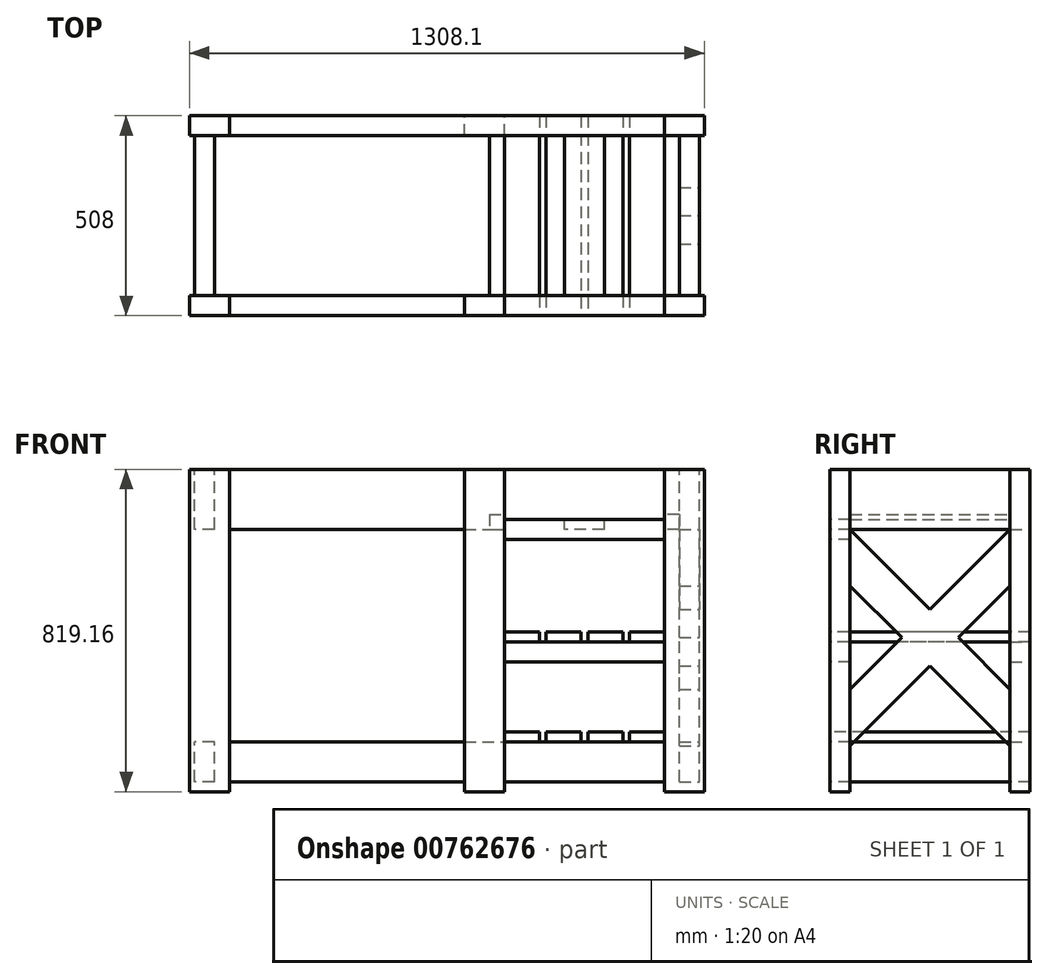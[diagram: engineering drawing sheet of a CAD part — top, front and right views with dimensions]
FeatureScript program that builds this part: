
annotation { "Feature Type Name" : "Feature", "Feature Type Description" : "" }
export const myFeature = defineFeature(function(context is Context, id is Id, definition is map)
    precondition{}
    {
        {
            var Q0;
            Q0=qCreatedBy(makeId("Right.planeOp"),FACE);
            var sketch = newSketch(context, id + "F0", { "sketchPlane" : qUnion([Q0])});
            skLineSegment(sketch, "E0.bottom", {"start": v(-254, 409.58) * mm, "end": v(-203.2, 409.58) * mm});
            skLineSegment(sketch, "E0.top", {"start": v(-254, -409.58) * mm, "end": v(-203.2, -409.58) * mm});
            skLineSegment(sketch, "E0.left", {"start": v(-254, 409.58) * mm, "end": v(-254, -409.58) * mm});
            skLineSegment(sketch, "E0.right", {"start": v(-203.2, 409.58) * mm, "end": v(-203.2, -409.58) * mm});
            skLineSegment(sketch, "E1.bottom", {"start": v(203.2, -409.58) * mm, "end": v(254, -409.58) * mm});
            skLineSegment(sketch, "E1.top", {"start": v(203.2, 409.58) * mm, "end": v(254, 409.58) * mm});
            skLineSegment(sketch, "E1.left", {"start": v(203.2, -409.58) * mm, "end": v(203.2, 409.58) * mm});
            skLineSegment(sketch, "E1.right", {"start": v(254, -409.58) * mm, "end": v(254, 409.58) * mm});
            skSolve(sketch);
        }
        {
            var Q0;
            Q0 = qSketchRegion(id + "F0", true);
            extrude(context, id + "F1", {"entities" : qUnion([Q0]), "depth" : 101.6 * mm, "offsetDistance" : 25.4 * mm});
        }
        {
            var Q0;
            Q0=makeQuery(id+"F1.opExtrude","SWEPT_FACE",FACE,{"disambiguationData":[OSD([sQuery(id+"F0.wireOp",EDGE,"E0.right")])]});
            var sketch = newSketch(context, id + "F2", { "sketchPlane" : qUnion([Q0])});
            skLineSegment(sketch, "E2.bottom", {"start": v(-88.9, 409.58) * mm, "end": v(-38.1, 409.58) * mm});
            skLineSegment(sketch, "E2.top", {"start": v(-88.9, 257.18) * mm, "end": v(-38.1, 257.18) * mm});
            skLineSegment(sketch, "E2.left", {"start": v(-88.9, 409.58) * mm, "end": v(-88.9, 257.18) * mm});
            skLineSegment(sketch, "E2.right", {"start": v(-38.1, 409.58) * mm, "end": v(-38.1, 257.18) * mm});
            skLineSegment(sketch, "E3.bottom", {"start": v(-88.9, -282.58) * mm, "end": v(-38.1, -282.58) * mm});
            skLineSegment(sketch, "E3.top", {"start": v(-88.9, -384.18) * mm, "end": v(-38.1, -384.18) * mm});
            skLineSegment(sketch, "E3.right", {"start": v(-38.1, -282.58) * mm, "end": v(-38.1, -384.18) * mm});
            skLineSegment(sketch, "E4", {"start": v(-88.9, -282.58) * mm, "end": v(-88.9, -384.18) * mm});
            skSolve(sketch);
        }
        {
            var Q0;
            Q0 = qSketchRegion(id + "F2", true);
            extrude(context, id + "F3", {"entities" : qUnion([Q0]), "endBound" : BoundingType.UP_TO_NEXT, "depth" : 25.4 * mm, "offsetDistance" : 25.4 * mm});
        }
        {
            var Q0;
            Q0=makeQuery(id+"F3.opExtrude","SWEPT_FACE",FACE,{"disambiguationData":[OSD([sQuery(id+"F2.wireOp",EDGE,"E2.left")])]});
            var sketch = newSketch(context, id + "F4", { "sketchPlane" : qUnion([Q0])});
            skLineSegment(sketch, "E5", {"start": v(-203.2, 257.18) * mm, "end": v(-203.2, 113.5) * mm});
            skLineSegment(sketch, "E6", {"start": v(-203.2, 113.5) * mm, "end": v(203.2, -292.9) * mm});
            skLineSegment(sketch, "E7", {"start": v(203.2, -292.9) * mm, "end": v(203.2, -149.22) * mm});
            skLineSegment(sketch, "E8", {"start": v(203.2, -149.22) * mm, "end": v(-203.2, 257.18) * mm});
            skLineSegment(sketch, "E9", {"start": v(203.2, 257.18) * mm, "end": v(0, 53.98) * mm});
            skLineSegment(sketch, "E10", {"start": v(-203.2, -149.22) * mm, "end": v(-203.2, -292.9) * mm});
            skLineSegment(sketch, "E11", {"start": v(-203.2, -292.9) * mm, "end": v(0, -89.7) * mm});
            skLineSegment(sketch, "E12", {"start": v(203.2, 113.5) * mm, "end": v(203.2, 257.18) * mm});
            skLineSegment(sketch, "E13.trimOffspring", {"start": v(-71.84, -17.87) * mm, "end": v(-203.2, -149.22) * mm});
            skLineSegment(sketch, "E14.trimOffspring", {"start": v(71.84, -17.87) * mm, "end": v(203.2, 113.5) * mm});
            skSolve(sketch);
        }
        {
            var Q0;
            Q0 = qSketchRegion(id + "F4", true);
            extrude(context, id + "F5", {"entities" : qUnion([Q0]), "oppositeDirection" : true, "depth" : 50.8 * mm, "offsetDistance" : 25.4 * mm});
        }
        {
            var Q0;
            Q0=makeQuery(id+"F1.opExtrude","CAP_FACE",FACE,{"disambiguationData":[OSD([sQuery(id+"F0.wireOp",EDGE,"E0.bottom"),sQuery(id+"F0.wireOp",EDGE,"E0.top"),sQuery(id+"F0.wireOp",EDGE,"E0.left"),sQuery(id+"F0.wireOp",EDGE,"E0.right")])],"isStart":true});
            var sketch = newSketch(context, id + "F6", { "sketchPlane" : qUnion([Q0])});
            skLineSegment(sketch, "E15.bottom", {"start": v(203.2, -282.58) * mm, "end": v(254, -282.58) * mm});
            skLineSegment(sketch, "E15.top", {"start": v(203.2, -384.18) * mm, "end": v(254, -384.18) * mm});
            skLineSegment(sketch, "E15.left", {"start": v(203.2, -282.58) * mm, "end": v(203.2, -384.18) * mm});
            skLineSegment(sketch, "E15.right", {"start": v(254, -282.58) * mm, "end": v(254, -384.18) * mm});
            skLineSegment(sketch, "E16.bottom", {"start": v(-254, -282.58) * mm, "end": v(-203.2, -282.58) * mm});
            skLineSegment(sketch, "E16.top", {"start": v(-254, -384.18) * mm, "end": v(-203.2, -384.18) * mm});
            skLineSegment(sketch, "E16.left", {"start": v(-254, -282.58) * mm, "end": v(-254, -384.18) * mm});
            skLineSegment(sketch, "E16.right", {"start": v(-203.2, -282.58) * mm, "end": v(-203.2, -384.18) * mm});
            skSolve(sketch);
        }
        {
            var Q0;
            Q0=makeQuery(id+"F1.opExtrude","CAP_FACE",FACE,{"disambiguationData":[OSD([sQuery(id+"F0.wireOp",EDGE,"E0.bottom"),sQuery(id+"F0.wireOp",EDGE,"E0.top"),sQuery(id+"F0.wireOp",EDGE,"E0.left"),sQuery(id+"F0.wireOp",EDGE,"E0.right")])],"isStart":true});
            cPlane(context, id + "F7", {"entities" : qUnion([Q0]), "cplaneType" : CPlaneType.OFFSET, "offset" : 552.45 * mm, "width" : 152.4 * mm, "height" : 152.4 * mm});
        }
        {
            var Q0;
            Q0=makeQuery(id+"F1.opExtrude","SWEPT_BODY",BODY,{"disambiguationData":[OSD([sQuery(id+"F0.wireOp",EDGE,"E1.bottom"),sQuery(id+"F0.wireOp",EDGE,"E1.top"),sQuery(id+"F0.wireOp",EDGE,"E1.left"),sQuery(id+"F0.wireOp",EDGE,"E1.right")])]});
            var Q1;
            Q1=makeQuery(id+"F3.opExtrude","SWEPT_BODY",BODY,{"disambiguationData":[OSD([sQuery(id+"F2.wireOp",EDGE,"E2.bottom"),sQuery(id+"F2.wireOp",EDGE,"E2.top"),sQuery(id+"F2.wireOp",EDGE,"E2.left"),sQuery(id+"F2.wireOp",EDGE,"E2.right")])]});
            var Q2;
            Q2=makeQuery(id+"F1.opExtrude","SWEPT_BODY",BODY,{"disambiguationData":[OSD([sQuery(id+"F0.wireOp",EDGE,"E0.bottom"),sQuery(id+"F0.wireOp",EDGE,"E0.top"),sQuery(id+"F0.wireOp",EDGE,"E0.left"),sQuery(id+"F0.wireOp",EDGE,"E0.right")])]});
            var Q3;
            Q3=makeQuery(id+"F3.opExtrude","SWEPT_BODY",BODY,{"disambiguationData":[OSD([sQuery(id+"F2.wireOp",EDGE,"E3.bottom"),sQuery(id+"F2.wireOp",EDGE,"E3.top"),sQuery(id+"F2.wireOp",EDGE,"E3.right"),sQuery(id+"F2.wireOp",EDGE,"E4")])]});
            var Q4;
            Q4=qCreatedBy(id+"F7.planeOp",FACE);
            mirror(context, id + "F8", {"entities" : qUnion([Q0, Q1, Q2, Q3]), "mirrorPlane" : qUnion([Q4])});
        }
        {
            var Q0;
            Q0=makeQuery(id+"F1.opExtrude","CAP_FACE",FACE,{"disambiguationData":[OSD([sQuery(id+"F0.wireOp",EDGE,"E0.bottom"),sQuery(id+"F0.wireOp",EDGE,"E0.top"),sQuery(id+"F0.wireOp",EDGE,"E0.left"),sQuery(id+"F0.wireOp",EDGE,"E0.right")])],"isStart":true});
            var sketch = newSketch(context, id + "F9", { "sketchPlane" : qUnion([Q0])});
            skLineSegment(sketch, "E17.bottom", {"start": v(203.2, 282.58) * mm, "end": v(254, 282.58) * mm});
            skLineSegment(sketch, "E17.top", {"start": v(203.2, 231.78) * mm, "end": v(254, 231.78) * mm});
            skLineSegment(sketch, "E17.left", {"start": v(203.2, 282.58) * mm, "end": v(203.2, 231.78) * mm});
            skLineSegment(sketch, "E17.right", {"start": v(254, 282.58) * mm, "end": v(254, 231.78) * mm});
            skLineSegment(sketch, "E18.bottom", {"start": v(203.2, 409.58) * mm, "end": v(254, 409.58) * mm});
            skLineSegment(sketch, "E18.top", {"start": v(203.2, 384.18) * mm, "end": v(254, 384.18) * mm});
            skLineSegment(sketch, "E18.left", {"start": v(203.2, 409.58) * mm, "end": v(203.2, 384.18) * mm});
            skLineSegment(sketch, "E18.right", {"start": v(254, 409.58) * mm, "end": v(254, 384.18) * mm});
            skLineSegment(sketch, "E19.bottom", {"start": v(-254, 409.58) * mm, "end": v(-203.2, 409.58) * mm});
            skLineSegment(sketch, "E19.top", {"start": v(-254, 384.18) * mm, "end": v(-203.2, 384.18) * mm});
            skLineSegment(sketch, "E19.left", {"start": v(-254, 409.58) * mm, "end": v(-254, 384.18) * mm});
            skLineSegment(sketch, "E19.right", {"start": v(-203.2, 409.58) * mm, "end": v(-203.2, 384.18) * mm});
            skPoint(sketch, "E20", {"position": v(254, 257.18) * mm});
            skLineSegment(sketch, "E21.bottom", {"start": v(203.2, -28.57) * mm, "end": v(254, -28.57) * mm});
            skLineSegment(sketch, "E21.top", {"start": v(203.2, -79.37) * mm, "end": v(254, -79.37) * mm});
            skLineSegment(sketch, "E21.left", {"start": v(203.2, -28.57) * mm, "end": v(203.2, -79.37) * mm});
            skLineSegment(sketch, "E21.right", {"start": v(254, -28.57) * mm, "end": v(254, -79.37) * mm});
            skLineSegment(sketch, "E22.bottom", {"start": v(-203.2, -28.57) * mm, "end": v(-254, -28.57) * mm});
            skLineSegment(sketch, "E22.top", {"start": v(-203.2, -79.37) * mm, "end": v(-254, -79.37) * mm});
            skLineSegment(sketch, "E22.left", {"start": v(-203.2, -28.57) * mm, "end": v(-203.2, -79.37) * mm});
            skLineSegment(sketch, "E22.right", {"start": v(-254, -28.57) * mm, "end": v(-254, -79.37) * mm});
            skSolve(sketch);
        }
        {
            var Q0;
            Q0=makeQuery(id+"F9.imprint","IMPRINT",FACE,{"disambiguationData":[TD([[makeQuery(id+"F9.imprint","IMPRINT",EDGE,{"derivedFrom":sQuery(id+"F9.wireOp",EDGE,"KkQRvC9S-9GU5-1TNo-BgkX-bVCRlUlDrE3p.bottom")}),-1.0]])]});
            var Q1;
            Q1=makeQuery(id+"F9.imprint","IMPRINT",FACE,{"disambiguationData":[TD([[makeQuery(id+"F9.imprint","IMPRINT",EDGE,{"derivedFrom":sQuery(id+"F9.wireOp",EDGE,"E17.bottom")}),-1.0]])]});
            var Q2;
            Q2=makeQuery(id+"F9.imprint","IMPRINT",FACE,{"disambiguationData":[TD([[makeQuery(id+"F9.imprint","IMPRINT",EDGE,{"derivedFrom":sQuery(id+"F9.wireOp",EDGE,"E21.bottom")}),-1.0]])]});
            var Q3;
            Q3=makeQuery(id+"F9.imprint","IMPRINT",FACE,{"disambiguationData":[TD([[makeQuery(id+"F9.imprint","IMPRINT",EDGE,{"derivedFrom":sQuery(id+"F9.wireOp",EDGE,"E22.bottom")}),1.0]])]});
            extrude(context, id + "F10", {"entities" : qUnion([Q0, Q1, Q2, Q3]), "depth" : 406.4 * mm, "offsetDistance" : 25.4 * mm});
        }
        {
            var Q0;
            Q0=makeQuery(id+"F10.opExtrude","CAP_FACE",FACE,{"disambiguationData":[OSD([sQuery(id+"F9.wireOp",EDGE,"E17.bottom"),sQuery(id+"F9.wireOp",EDGE,"E17.top"),sQuery(id+"F9.wireOp",EDGE,"E17.left"),sQuery(id+"F9.wireOp",EDGE,"E17.right")])],"isStart":false});
            var sketch = newSketch(context, id + "F11", { "sketchPlane" : qUnion([Q0])});
            skLineSegment(sketch, "E23.top", {"start": v(254, 409.58) * mm, "end": v(203.2, 409.58) * mm});
            skLineSegment(sketch, "E23.left", {"start": v(254, -409.58) * mm, "end": v(254, 409.57) * mm});
            skLineSegment(sketch, "E23.right", {"start": v(203.2, -409.58) * mm, "end": v(203.2, 409.58) * mm});
            skLineSegment(sketch, "E24.bottom", {"start": v(-203.2, -282.58) * mm, "end": v(-254, -282.58) * mm});
            skLineSegment(sketch, "E24.top", {"start": v(-203.2, 257.18) * mm, "end": v(-254, 257.18) * mm});
            skLineSegment(sketch, "E24.left", {"start": v(-203.2, -282.58) * mm, "end": v(-203.2, 257.18) * mm});
            skLineSegment(sketch, "E24.right", {"start": v(-254, -282.58) * mm, "end": v(-254, 257.18) * mm});
            skLineSegment(sketch, "E25", {"start": v(203.2, -409.58) * mm, "end": v(254, -409.58) * mm});
            skSolve(sketch);
        }
        {
            var Q0;
            Q0=makeQuery(id+"F6.imprint","IMPRINT",FACE,{"disambiguationData":[TD([[makeQuery(id+"F6.imprint","IMPRINT",EDGE,{"derivedFrom":sQuery(id+"F6.wireOp",EDGE,"E16.bottom")}),-1.0]])]});
            extrude(context, id + "F12", {"entities" : qUnion([Q0]), "endBound" : BoundingType.UP_TO_NEXT, "depth" : 25.4 * mm, "offsetDistance" : 25.4 * mm});
        }
        {
            var Q0;
            Q0 = qSketchRegion(id + "F11", true);
            extrude(context, id + "F13", {"entities" : qUnion([Q0]), "depth" : 101.6 * mm, "offsetDistance" : 25.4 * mm});
        }
        {
            var Q0;
            Q0=makeQuery(id+"Fzglu1UX7R0Jx5i_16.boolean.opBoolean","MERGE",FACE,{"derivedFrom":[makeQuery(id+"F1.opExtrude","SWEPT_FACE",FACE,{"disambiguationData":[OSD([sQuery(id+"F0.wireOp",EDGE,"E0.left")])]}),makeQuery(id+"Fzglu1UX7R0Jx5i_16.opExtrude","SWEPT_FACE",FACE,{"disambiguationData":[OSD([sQuery(id+"F6.wireOp",EDGE,"E15.right")])]})]});
            var sketch = newSketch(context, id + "F14", { "sketchPlane" : qUnion([Q0])});
            skLineSegment(sketch, "E26.bottom", {"start": v(0, -3.17) * mm, "end": v(-88.9, -3.17) * mm});
            skLineSegment(sketch, "E26.top", {"start": v(0, -28.57) * mm, "end": v(-88.9, -28.57) * mm});
            skLineSegment(sketch, "E26.left", {"start": v(0, -3.17) * mm, "end": v(0, -28.57) * mm});
            skLineSegment(sketch, "E26.right", {"start": v(-406.4, -3.17) * mm, "end": v(-406.4, -28.57) * mm});
            skLineSegment(sketch, "E27", {"start": v(-317.5, -3.17) * mm, "end": v(-317.5, -28.57) * mm});
            skLineSegment(sketch, "E28", {"start": v(-300.35, -3.17) * mm, "end": v(-300.35, -28.57) * mm});
            skLineSegment(sketch, "E29", {"start": v(-211.45, -3.17) * mm, "end": v(-211.45, -28.57) * mm});
            skLineSegment(sketch, "E30", {"start": v(-194.3, -3.17) * mm, "end": v(-194.3, -28.57) * mm});
            skLineSegment(sketch, "E31", {"start": v(-105.4, -3.17) * mm, "end": v(-105.4, -28.57) * mm});
            skLineSegment(sketch, "E32", {"start": v(-88.9, -3.17) * mm, "end": v(-88.9, -28.57) * mm});
            skLineSegment(sketch, "E33.trimOffspring", {"start": v(-317.5, -3.17) * mm, "end": v(-406.4, -3.17) * mm});
            skLineSegment(sketch, "E34.trimOffspring", {"start": v(-317.5, -28.57) * mm, "end": v(-406.4, -28.57) * mm});
            skLineSegment(sketch, "E35.trimOffspring", {"start": v(-211.45, -3.17) * mm, "end": v(-300.35, -3.17) * mm});
            skLineSegment(sketch, "E36.trimOffspring", {"start": v(-211.45, -28.57) * mm, "end": v(-300.35, -28.57) * mm});
            skLineSegment(sketch, "E37.trimOffspring", {"start": v(-105.4, -3.17) * mm, "end": v(-194.3, -3.17) * mm});
            skLineSegment(sketch, "E38.trimOffspring", {"start": v(-105.4, -28.57) * mm, "end": v(-194.3, -28.57) * mm});
            skLineSegment(sketch, "E39.bottom", {"start": v(0, -257.18) * mm, "end": v(-88.9, -257.18) * mm});
            skLineSegment(sketch, "E39.top", {"start": v(0, -282.58) * mm, "end": v(-88.9, -282.58) * mm});
            skLineSegment(sketch, "E39.left", {"start": v(0, -257.18) * mm, "end": v(0, -282.58) * mm});
            skLineSegment(sketch, "E39.right", {"start": v(-406.4, -257.18) * mm, "end": v(-406.4, -282.58) * mm});
            skLineSegment(sketch, "E40", {"start": v(-317.5, -257.18) * mm, "end": v(-317.5, -282.58) * mm});
            skLineSegment(sketch, "E41", {"start": v(-300.35, -257.18) * mm, "end": v(-300.35, -282.58) * mm});
            skLineSegment(sketch, "E42", {"start": v(-211.45, -257.18) * mm, "end": v(-211.45, -282.58) * mm});
            skLineSegment(sketch, "E43", {"start": v(-194.3, -257.18) * mm, "end": v(-194.3, -282.58) * mm});
            skLineSegment(sketch, "E44", {"start": v(-105.4, -257.18) * mm, "end": v(-105.4, -282.58) * mm});
            skLineSegment(sketch, "E45", {"start": v(-88.9, -257.18) * mm, "end": v(-88.9, -282.58) * mm});
            skLineSegment(sketch, "E46.trimOffspring", {"start": v(-317.5, -257.18) * mm, "end": v(-406.4, -257.18) * mm});
            skLineSegment(sketch, "E47.trimOffspring", {"start": v(-317.5, -282.58) * mm, "end": v(-406.4, -282.58) * mm});
            skLineSegment(sketch, "E48.trimOffspring", {"start": v(-211.45, -257.18) * mm, "end": v(-300.35, -257.18) * mm});
            skLineSegment(sketch, "E49.trimOffspring", {"start": v(-211.45, -282.58) * mm, "end": v(-300.35, -282.58) * mm});
            skLineSegment(sketch, "E50.trimOffspring", {"start": v(-105.4, -257.18) * mm, "end": v(-194.3, -257.18) * mm});
            skLineSegment(sketch, "E51.trimOffspring", {"start": v(-105.4, -282.58) * mm, "end": v(-194.3, -282.58) * mm});
            skSolve(sketch);
        }
        {
            var Q0;
            Q0 = qSketchRegion(id + "F14", true);
            var Q1;
            Q1=makeQuery(id+"F1.opExtrude","SWEPT_FACE",FACE,{"disambiguationData":[OSD([sQuery(id+"F0.wireOp",EDGE,"E1.right")])]});
            extrude(context, id + "F15", {"entities" : qUnion([Q0]), "endBound" : BoundingType.UP_TO_SURFACE, "oppositeDirection" : true, "depth" : 25.4 * mm, "endBoundEntityFace" : qUnion([Q1]), "offsetDistance" : 25.4 * mm});
        }
        {
            var Q0;
            Q0=makeQuery(id+"F6.imprint","IMPRINT",FACE,{"disambiguationData":[TD([[makeQuery(id+"F6.imprint","IMPRINT",EDGE,{"derivedFrom":sQuery(id+"F6.wireOp",EDGE,"E15.bottom")}),-1.0]])]});
            extrude(context, id + "F16", {"entities" : qUnion([Q0]), "endBound" : BoundingType.UP_TO_NEXT, "depth" : 25.4 * mm, "offsetDistance" : 25.4 * mm});
        }
        {
            var Q0;
            Q0=makeQuery(id+"F8.opPattern","COPY",FACE,{"derivedFrom":makeQuery(id+"F1.opExtrude","CAP_FACE",FACE,{"disambiguationData":[OSD([sQuery(id+"F0.wireOp",EDGE,"E0.bottom"),sQuery(id+"F0.wireOp",EDGE,"E0.top"),sQuery(id+"F0.wireOp",EDGE,"E0.left"),sQuery(id+"F0.wireOp",EDGE,"E0.right")])],"isStart":true}),"instanceName":"1"});
            var sketch = newSketch(context, id + "F17", { "sketchPlane" : qUnion([Q0])});
            skLineSegment(sketch, "E52.bottom", {"start": v(-254, 257.18) * mm, "end": v(-203.2, 257.18) * mm});
            skLineSegment(sketch, "E52.top", {"start": v(-254, 409.58) * mm, "end": v(-203.2, 409.58) * mm});
            skLineSegment(sketch, "E52.left", {"start": v(-254, 257.18) * mm, "end": v(-254, 409.58) * mm});
            skLineSegment(sketch, "E53.bottom", {"start": v(203.2, 409.58) * mm, "end": v(254, 409.58) * mm});
            skLineSegment(sketch, "E53.top", {"start": v(203.2, 257.18) * mm, "end": v(254, 257.18) * mm});
            skLineSegment(sketch, "E53.left", {"start": v(203.2, 409.58) * mm, "end": v(203.2, 257.18) * mm});
            skLineSegment(sketch, "E53.right", {"start": v(254, 409.58) * mm, "end": v(254, 257.18) * mm});
            skSolve(sketch);
        }
        {
            var Q0;
            Q0=makeQuery(id+"F17.imprint","IMPRINT",FACE,{"disambiguationData":[TD([[makeQuery(id+"F17.imprint","IMPRINT",EDGE,{"derivedFrom":sQuery(id+"F17.wireOp",EDGE,"E52.bottom")}),1.0]])]});
            extrude(context, id + "F18", {"entities" : qUnion([Q0]), "endBound" : BoundingType.UP_TO_NEXT, "depth" : 25.4 * mm, "offsetDistance" : 25.4 * mm});
        }
        {
            var Q0;
            Q0=makeQuery(id+"F17.imprint","IMPRINT",FACE,{"disambiguationData":[TD([[makeQuery(id+"F17.imprint","IMPRINT",EDGE,{"derivedFrom":sQuery(id+"F17.wireOp",EDGE,"E53.bottom")}),-1.0]])]});
            extrude(context, id + "F19", {"entities" : qUnion([Q0]), "endBound" : BoundingType.UP_TO_NEXT, "depth" : 25.4 * mm, "offsetDistance" : 25.4 * mm});
        }
        {
            var Q0;
            Q0=makeQuery(id+"F19.opExtrude","SWEPT_FACE",FACE,{"disambiguationData":[OSD([sQuery(id+"F17.wireOp",EDGE,"E53.left")])]});
            var sketch = newSketch(context, id + "F20", { "sketchPlane" : qUnion([Q0])});
            skLineSegment(sketch, "E54.bottom", {"start": v(-254, 257.18) * mm, "end": v(-152.4, 257.18) * mm});
            skLineSegment(sketch, "E54.top", {"start": v(-254, 282.58) * mm, "end": v(-152.4, 282.58) * mm});
            skLineSegment(sketch, "E54.left", {"start": v(-254, 257.18) * mm, "end": v(-254, 282.58) * mm});
            skLineSegment(sketch, "E54.right", {"start": v(-152.4, 257.18) * mm, "end": v(-152.4, 282.58) * mm});
            skPoint(sketch, "E55", {"position": v(-203.2, 282.58) * mm});
            skLineSegment(sketch, "E56.bottom", {"start": v(0, 257.18) * mm, "end": v(38.1, 257.18) * mm});
            skLineSegment(sketch, "E56.top", {"start": v(0, 295.28) * mm, "end": v(38.1, 295.28) * mm});
            skLineSegment(sketch, "E56.left", {"start": v(0, 257.18) * mm, "end": v(0, 295.28) * mm});
            skLineSegment(sketch, "E56.right", {"start": v(38.1, 257.18) * mm, "end": v(38.1, 295.28) * mm});
            skLineSegment(sketch, "E57.bottom", {"start": v(-406.4, 257.18) * mm, "end": v(-444.5, 257.18) * mm});
            skLineSegment(sketch, "E57.top", {"start": v(-406.4, 295.28) * mm, "end": v(-444.5, 295.28) * mm});
            skLineSegment(sketch, "E57.left", {"start": v(-406.4, 257.18) * mm, "end": v(-406.4, 295.28) * mm});
            skLineSegment(sketch, "E57.right", {"start": v(-444.5, 257.18) * mm, "end": v(-444.5, 295.28) * mm});
            skSolve(sketch);
        }
        {
            var Q0;
            Q0 = qSketchRegion(id + "F20", true);
            extrude(context, id + "F21", {"entities" : qUnion([Q0]), "endBound" : BoundingType.UP_TO_NEXT, "depth" : 25.4 * mm, "offsetDistance" : 25.4 * mm});
        }
    });
